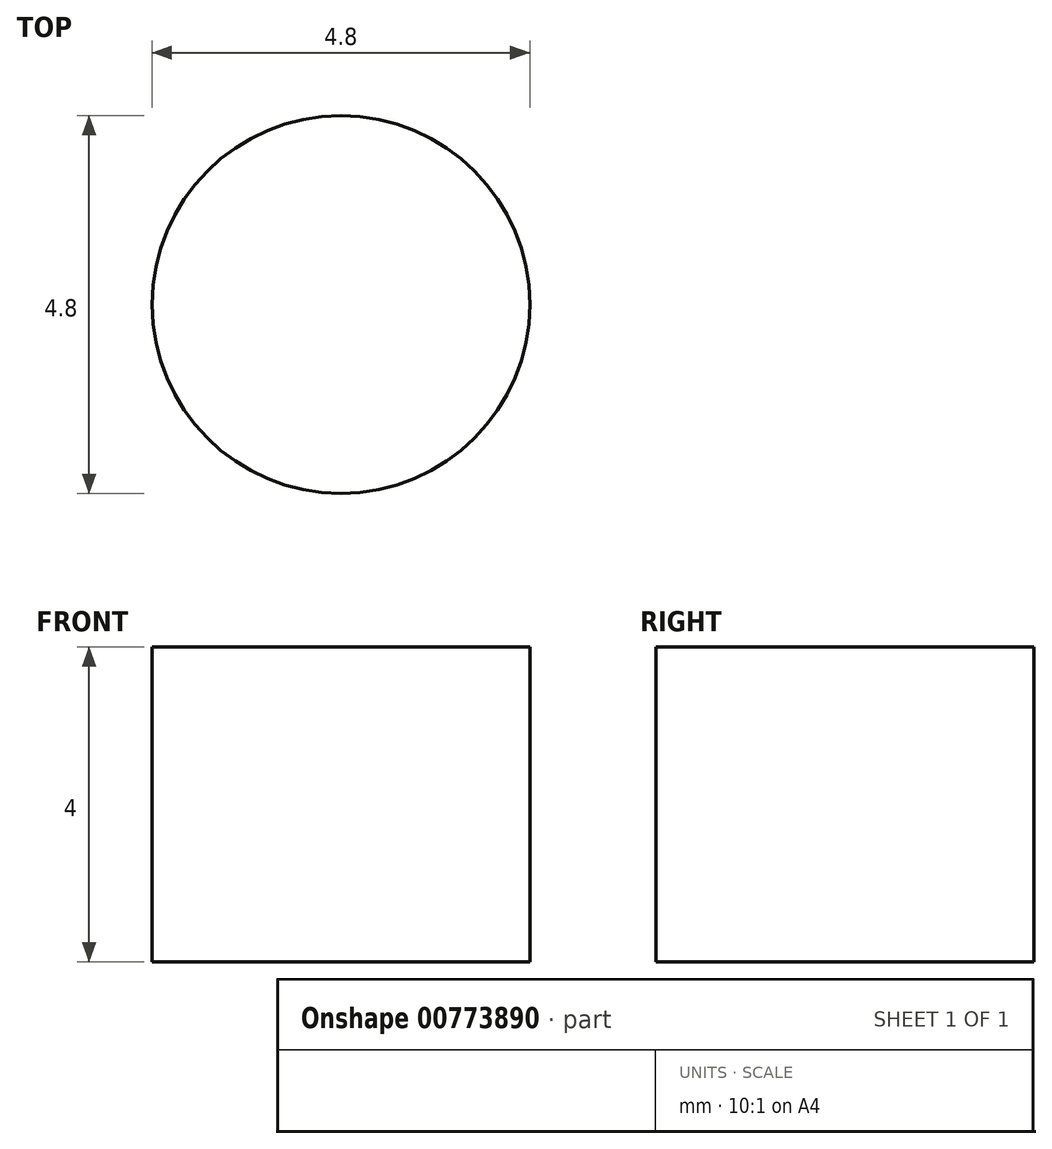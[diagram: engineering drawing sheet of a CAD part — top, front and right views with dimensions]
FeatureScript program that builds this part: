
annotation { "Feature Type Name" : "Feature", "Feature Type Description" : "" }
export const myFeature = defineFeature(function(context is Context, id is Id, definition is map)
    precondition{}
    {
        {
            var Q0;
            Q0=qCreatedBy(makeId("Top.planeOp"),FACE);
            var sketch = newSketch(context, id + "F0", { "sketchPlane" : qUnion([Q0])});
            skCircle(sketch, "E0", {"center": v(0, 0) * mm, "radius": 2.4 * mm});
            skSolve(sketch);
        }
        {
            var Q0;
            Q0=makeQuery(id+"F0.imprint","IMPRINT",FACE,{"disambiguationData":[TD([[makeQuery(id+"F0.imprint","IMPRINT",EDGE,{"derivedFrom":sQuery(id+"F0.wireOp",EDGE,"E0")}),1.0]])]});
            extrude(context, id + "F1", {"entities" : qUnion([Q0]), "depth" : 4 * mm, "offsetDistance" : 25 * mm});
        }
    });
